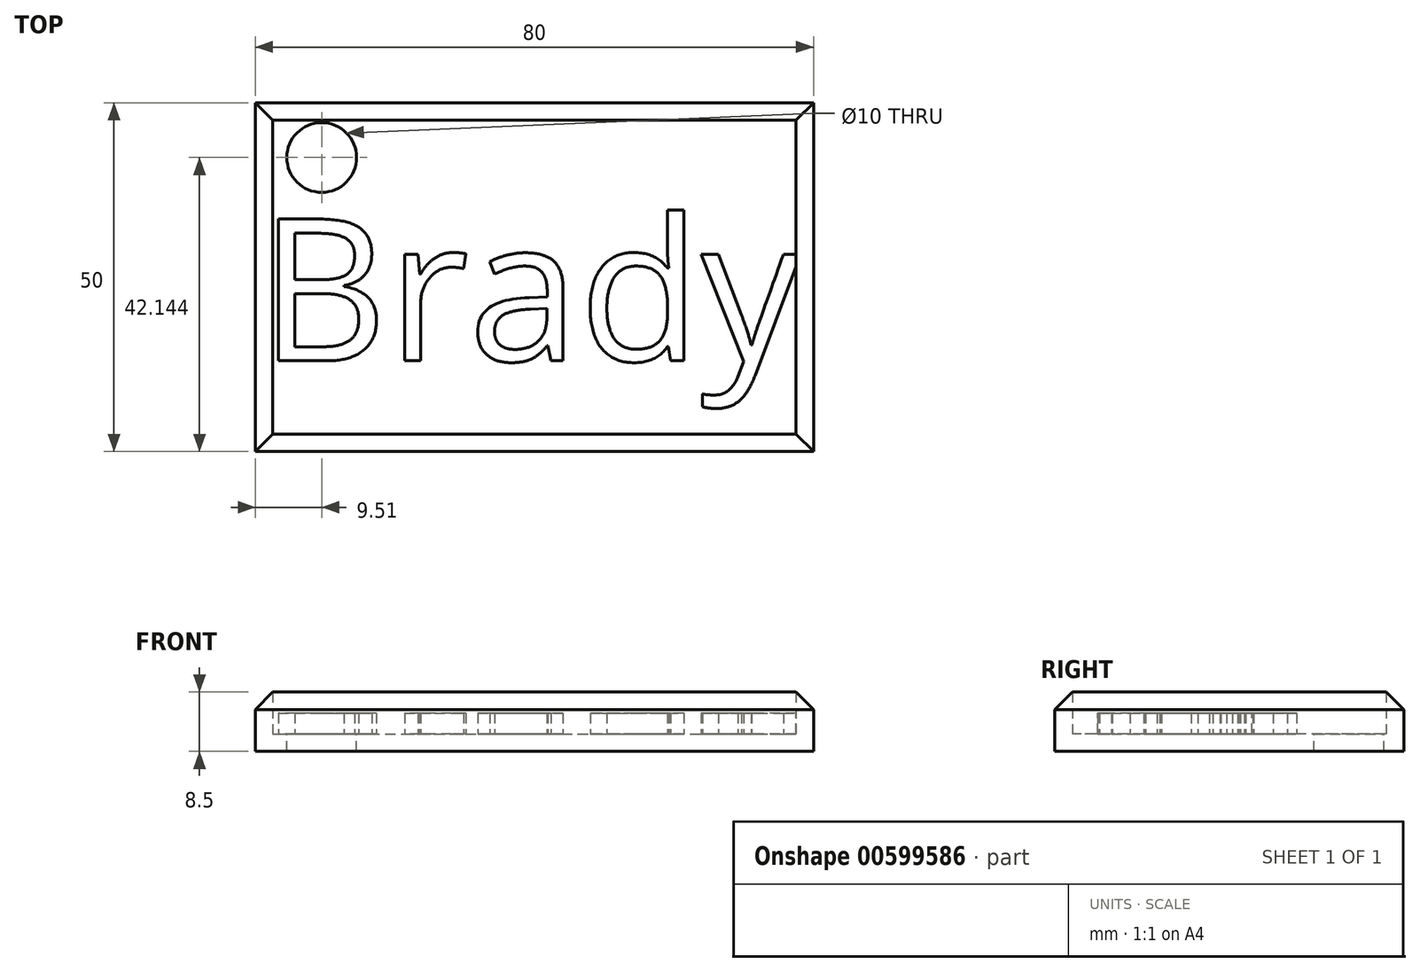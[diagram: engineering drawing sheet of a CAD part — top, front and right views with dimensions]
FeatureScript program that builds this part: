
annotation { "Feature Type Name" : "Feature", "Feature Type Description" : "" }
export const myFeature = defineFeature(function(context is Context, id is Id, definition is map)
    precondition{}
    {
        {
            var Q0;
            Q0=qCreatedBy(makeId("Top.planeOp"),FACE);
            var sketch = newSketch(context, id + "F0", { "sketchPlane" : qUnion([Q0])});
            skLineSegment(sketch, "E0.bottom", {"start": v(0, 0) * mm, "end": v(80, 0) * mm});
            skLineSegment(sketch, "E0.top", {"start": v(0, -50) * mm, "end": v(80, -50) * mm});
            skLineSegment(sketch, "E0.left", {"start": v(0, 0) * mm, "end": v(0, -50) * mm});
            skLineSegment(sketch, "E0.right", {"start": v(80, 0) * mm, "end": v(80, -50) * mm});
            skSolve(sketch);
        }
        {
            var Q0;
            Q0=makeQuery(id+"F0.imprint","IMPRINT",FACE,{"disambiguationData":[TD([[makeQuery(id+"F0.imprint","IMPRINT",EDGE,{"derivedFrom":sQuery(id+"F0.wireOp",EDGE,"E0.bottom")}),-1.0]])]});
            extrude(context, id + "F1", {"entities" : qUnion([Q0]), "depth" : 11 * mm, "offsetDistance" : 25 * mm});
        }
        {
            var Q0;
            Q0=makeQuery(id+"F1.opExtrude","CAP_FACE",FACE,{"disambiguationData":[OSD([sQuery(id+"F0.wireOp",EDGE,"E0.bottom"),sQuery(id+"F0.wireOp",EDGE,"E0.top"),sQuery(id+"F0.wireOp",EDGE,"E0.left"),sQuery(id+"F0.wireOp",EDGE,"E0.right")])],"isStart":false});
            shell(context, id + "F2", {"entities" : qUnion([Q0]), "thickness" : 2.5 * mm});
        }
        {
            var Q0;
            Q0=makeQuery(id+"F2.opShell","OFFSET_FACE",FACE,{"disambiguationData":[OSD([sQuery(id+"F0.wireOp",EDGE,"E0.bottom"),sQuery(id+"F0.wireOp",EDGE,"E0.top"),sQuery(id+"F0.wireOp",EDGE,"E0.left"),sQuery(id+"F0.wireOp",EDGE,"E0.right")])]});
            var sketch = newSketch(context, id + "F3", { "sketchPlane" : qUnion([Q0])});
            skCircle(sketch, "E1", {"center": v(9.51, -7.86) * mm, "radius": 5.83 * mm});
            skSolve(sketch);
        }
        {
            var Q0;
            Q0=sQuery(id+"F3.wireOp",VERTEX,"E1.center");
            var Q1;
            Q1=makeQuery(id+"F1.opExtrude","SWEPT_BODY",BODY,{"disambiguationData":[OSD([sQuery(id+"F0.wireOp",EDGE,"E0.bottom"),sQuery(id+"F0.wireOp",EDGE,"E0.top"),sQuery(id+"F0.wireOp",EDGE,"E0.left"),sQuery(id+"F0.wireOp",EDGE,"E0.right")])]});
            hole(context, id + "F4", {"style" : HoleStyle.SIMPLE, "endStyle" : HoleEndStyle.THROUGH, "holeDiameter" : 10 * mm, "majorDiameter" : 5 * mm, "isTappedThrough" : true, "tappedDepth" : 12 * mm, "tapClearance" : 3, "locations" : qUnion([Q0]), "scope" : qUnion([Q1])});
        }
        {
            var Q0;
            Q0=makeQuery(id+"F2.opShell","OFFSET_FACE",FACE,{"disambiguationData":[OSD([sQuery(id+"F0.wireOp",EDGE,"E0.bottom"),sQuery(id+"F0.wireOp",EDGE,"E0.top"),sQuery(id+"F0.wireOp",EDGE,"E0.left"),sQuery(id+"F0.wireOp",EDGE,"E0.right")])]});
            var sketch = newSketch(context, id + "F5", { "sketchPlane" : qUnion([Q0])});
            skText(sketch, "E2", { "text": "Brady", "fontName": "OpenSans-Regular.ttf"});
            const initialGuessF5  = {"E2": [0.00048, -0.037, 1, 0, 0.0205]};
            skSetInitialGuess(sketch, initialGuessF5);
            skSolve(sketch);
        }
        {
            var Q0;
            Q0 = qSketchRegion(id + "F5", true);
            extrude(context, id + "F6", {"entities" : qUnion([Q0]), "operationType" : NewBodyOperationType.ADD, "depth" : 3 * mm, "offsetDistance" : 25 * mm});
        }
        {
            var Q0;
            Q0=makeQuery(id+"F1.opExtrude","CAP_EDGE",EDGE,{"disambiguationData":[OSD([sQuery(id+"F0.wireOp",EDGE,"E0.left")])],"isStart":false});
            var Q1;
            Q1=makeQuery(id+"F1.opExtrude","CAP_EDGE",EDGE,{"disambiguationData":[OSD([sQuery(id+"F0.wireOp",EDGE,"E0.bottom")])],"isStart":false});
            var Q2;
            Q2=makeQuery(id+"F1.opExtrude","CAP_EDGE",EDGE,{"disambiguationData":[OSD([sQuery(id+"F0.wireOp",EDGE,"E0.right")])],"isStart":false});
            var Q3;
            Q3=makeQuery(id+"F1.opExtrude","CAP_EDGE",EDGE,{"disambiguationData":[OSD([sQuery(id+"F0.wireOp",EDGE,"E0.top")])],"isStart":false});
            chamfer(context, id + "F7", {"entities" : qUnion([Q0, Q1, Q2, Q3]), "width" : 5 * mm, "tangentPropagation" : true});
        }
    });
